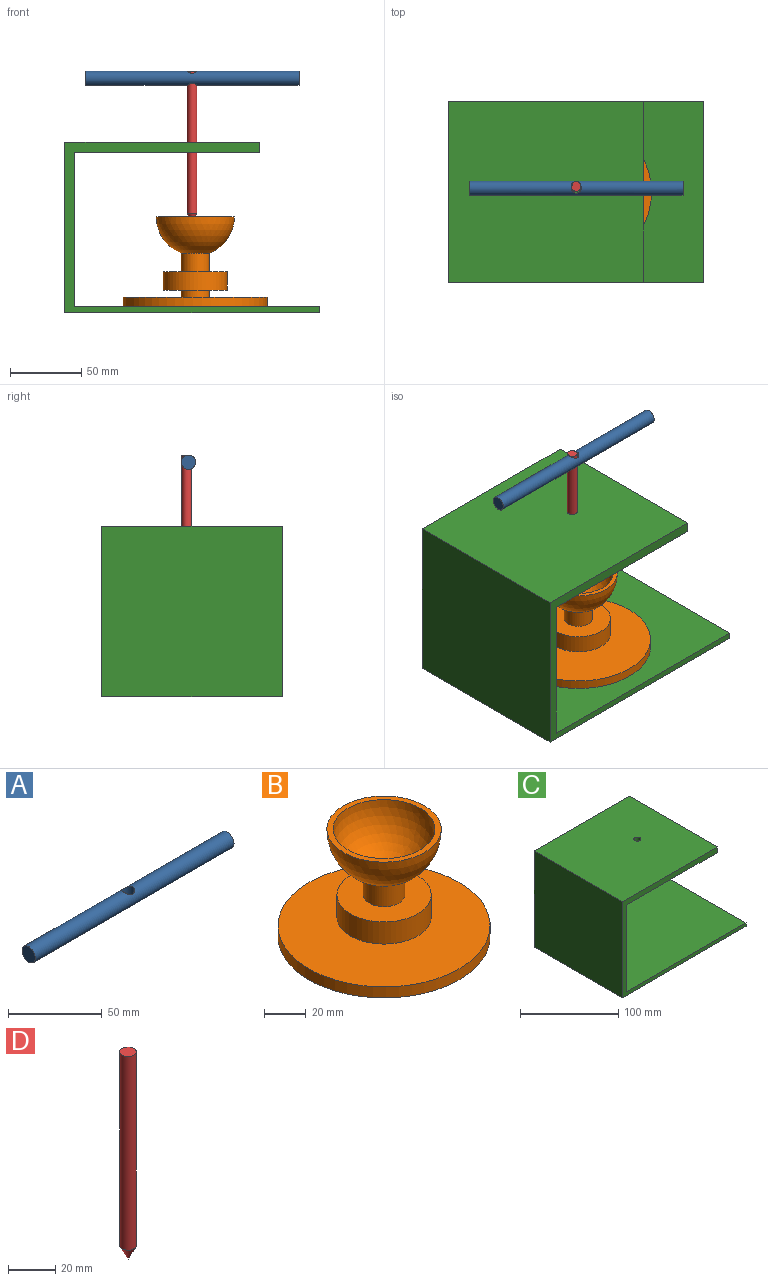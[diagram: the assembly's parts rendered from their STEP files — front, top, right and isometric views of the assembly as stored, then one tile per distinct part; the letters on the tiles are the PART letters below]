
ASSEMBLY  parts=4 mates=3
PART A: 4 faces, bbox 150x10x10 mm
  f0: cylinder r=5mm len=150mm, axis (-1,0,0), area 4629.5mm2, adj f1,f2,f3
  f1: plane 10x10mm, normal (1,0,0), area 78.5mm2, adj f0
  f2: plane 10x10mm, normal (-1,0,0), area 78.5mm2, adj f0
  f3: cylinder r=3.5mm len=10mm, axis (0,0,1), area 189.8mm2, adj f0
PART B: 11 faces, bbox 101.6x101.6x63.1 mm
  f0: plane 101.6x101.6mm, normal (0,0,-1), area 8106.6mm2, adj f1
  f1: cylinder r=50.8mm len=101.6mm, axis (0,0,1), area 2066.8mm2, adj f0,f2
  f2: plane 101.6x101.6mm, normal (0,0,1), area 7796.9mm2, adj f1,f3
  f3: cylinder r=9.93mm len=19.86mm, axis (0,0,1), area 323.2mm2, adj f2,f4
  f4: plane 45.19x45.19mm, normal (0,0,-1), area 1293.8mm2, adj f3,f5
  f5: cylinder r=22.59mm len=45.19mm, axis (0,0,1), area 1838.5mm2, adj f4,f6
  f6: plane 45.19x45.19mm, normal (0,0,1), area 1293.8mm2, adj f5,f7
  f7: cylinder r=9.93mm len=19.86mm, axis (0,0,1), area 808mm2, adj f6,f8
  f8: sphere r=27.43mm, area 4405.6mm2, adj f7,f9
  f9: plane 54.85x54.85mm, normal (0,0,1), area 488.5mm2, adj f8,f10
  f10: sphere r=24.43mm, area 3749.1mm2, adj f9
PART C: 11 faces, bbox 178.7x127x120 mm
  f0: plane 127x4.4mm, normal (1,0,0), area 558.5mm2, adj f1,f7,f8,f9
  f1: plane 172.22x127mm, normal (0,0,1), area 21872.5mm2, adj f0,f2,f8,f9
  f2: plane 127x108.38mm, normal (1,0,0), area 13763.9mm2, adj f1,f3,f8,f9
  f3: plane 130.59x127mm, normal (0,0,-1), area 16545.9mm2, adj f2,f4,f8,f9,f10
  f4: plane 127x7.23mm, normal (1,0,0), area 917.6mm2, adj f3,f5,f8,f9
  f5: plane 137.02x127mm, normal (0,0,1), area 17363.3mm2, adj f4,f6,f8,f9,f10
  f6: plane 127x120mm, normal (-1,0,0), area 15240mm2, adj f5,f7,f8,f9
  f7: plane 178.66x127mm, normal (0,0,-1), area 22689.9mm2, adj f0,f6,f8,f9
  f8: plane 178.66x120mm, normal (0,-1,0), area 2473.2mm2, adj f0,f1,f2,f3,f4,f5,f6,f7
  f9: plane 178.66x120mm, normal (0,1,0), area 2473.2mm2, adj f0,f1,f2,f3,f4,f5,f6,f7
  f10: cylinder r=3.5mm len=7.23mm, axis (0,0,-1), area 158.9mm2, adj f3,f5
PART D: 4 faces, bbox 7x7x107 mm
  f0: cylinder r=3.5mm len=100mm, axis (0,0,-1), area 2199.1mm2, adj f1,f2
  f1: plane 7x7mm, normal (0,0,1), area 38.5mm2, adj f0
  f2: plane 7x7mm, normal (0,0,-1), area 0.3mm2, adj f0,f3
  f3: cone r=0mm half-angle=26.6deg, axis (0,0,1), area 85.4mm2, adj f2
PLACE A t=(-133.1,-41.77,168.72)mm
PLACE B t=(-56.01,-44.26,8.19)mm
PLACE C t=(-58.3,19.24,3.79)mm
PLACE D t=(-58.3,-40.51,73.79)mm
MATE planar A.f3 <-> D.f0  axis (0,0,1) through (-58.1,-41.77,173.79)mm
MATE revolute D.f0 <-> C.f10  axis (0,0,-1) through (-58.3,-40.51,123.79)mm
MATE planar C.f1 <-> B.f1  axis (0,0,1) through (-55.08,-44.26,8.19)mm
